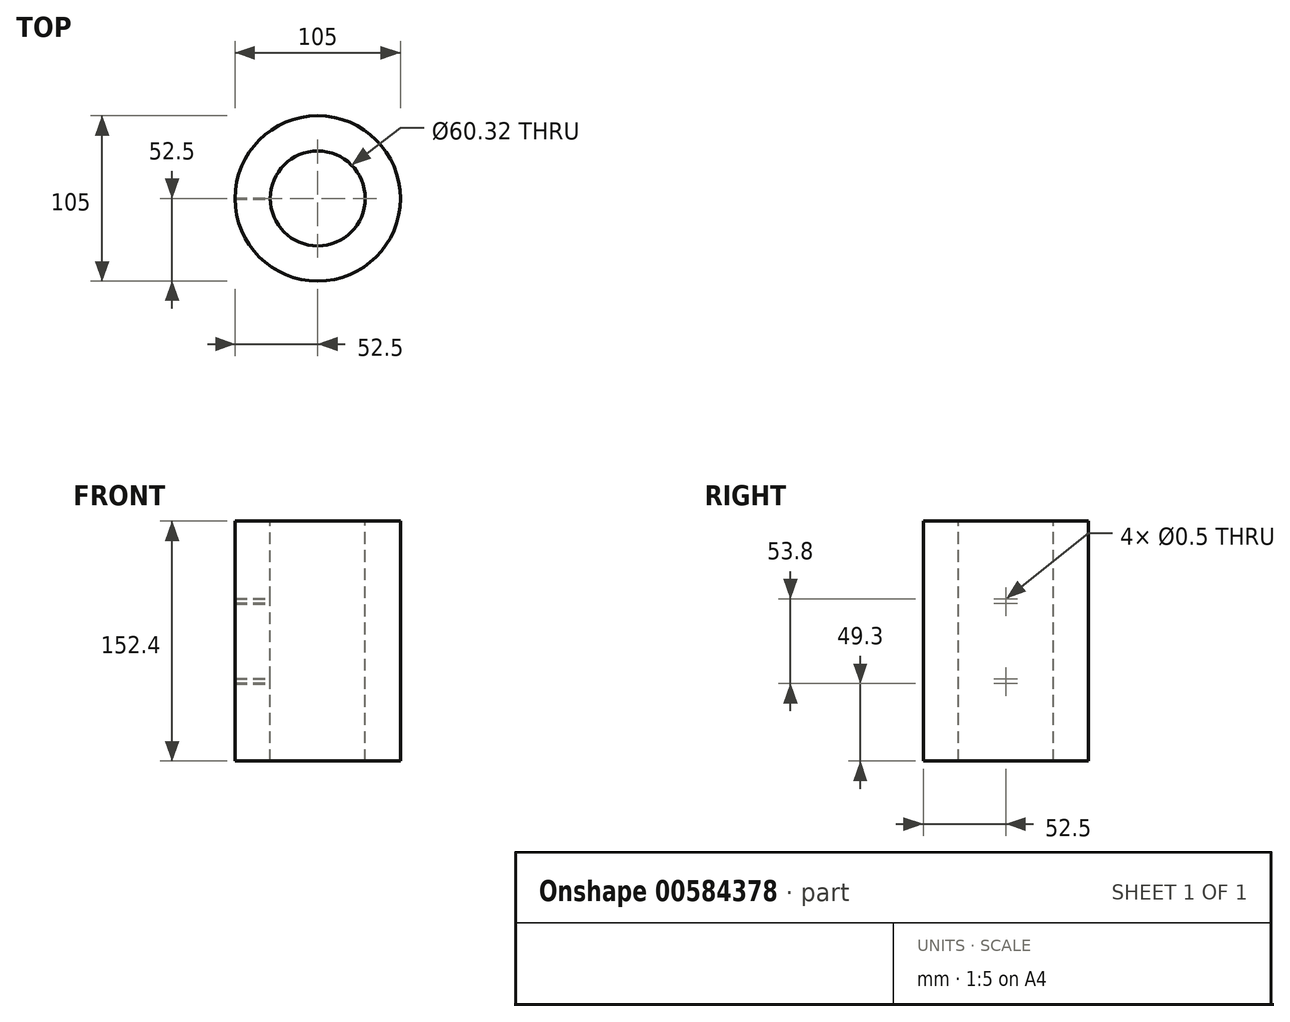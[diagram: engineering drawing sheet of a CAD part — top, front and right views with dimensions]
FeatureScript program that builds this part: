
annotation { "Feature Type Name" : "Feature", "Feature Type Description" : "" }
export const myFeature = defineFeature(function(context is Context, id is Id, definition is map)
    precondition{}
    {
        {
            var Q0;
            Q0=qCreatedBy(makeId("Top.planeOp"),FACE);
            var sketch = newSketch(context, id + "F0", { "sketchPlane" : qUnion([Q0])});
            skCircle(sketch, "E0", {"center": v(0, 0) * mm, "radius": 30.16 * mm});
            skCircle(sketch, "E1", {"center": v(0, 0) * mm, "radius": 52.5 * mm});
            skSolve(sketch);
        }
        {
            var Q0;
            Q0=makeQuery(id+"F0.imprint","IMPRINT",FACE,{"disambiguationData":[TD([[makeQuery(id+"F0.imprint","IMPRINT",EDGE,{"derivedFrom":sQuery(id+"F0.wireOp",EDGE,"E0")}),-1.0]])]});
            var Q1;
            Q1 = qSketchRegion(id + "F2", true);
            extrude(context, id + "F1", {"entities" : qUnion([Q0, Q1]), "oppositeDirection" : true, "depth" : 152.4 * mm, "offsetDistance" : 25.4 * mm});
        }
        {
            var Q0;
            Q0=qCreatedBy(makeId("Right.planeOp"),FACE);
            var sketch = newSketch(context, id + "F2", { "sketchPlane" : qUnion([Q0])});
            skLineSegment(sketch, "E2.left", {"start": v(0, 0) * mm, "end": v(0, -152.4) * mm});
            skCircle(sketch, "E3", {"center": v(0, -49.3) * mm, "radius": 0.25 * mm});
            skCircle(sketch, "E4", {"center": v(0, -52.3) * mm, "radius": 0.25 * mm});
            skCircle(sketch, "E5", {"center": v(0, -103.1) * mm, "radius": 0.25 * mm});
            skCircle(sketch, "E6", {"center": v(0, -100.1) * mm, "radius": 0.25 * mm});
            skSolve(sketch);
        }
        {
            var Q0;
            Q0 = qSketchRegion(id + "F2", true);
            extrude(context, id + "F3", {"entities" : qUnion([Q0]), "operationType" : NewBodyOperationType.REMOVE, "endBound" : BoundingType.THROUGH_ALL, "oppositeDirection" : true, "depth" : 25.4 * mm, "offsetDistance" : 25.4 * mm});
        }
    });
